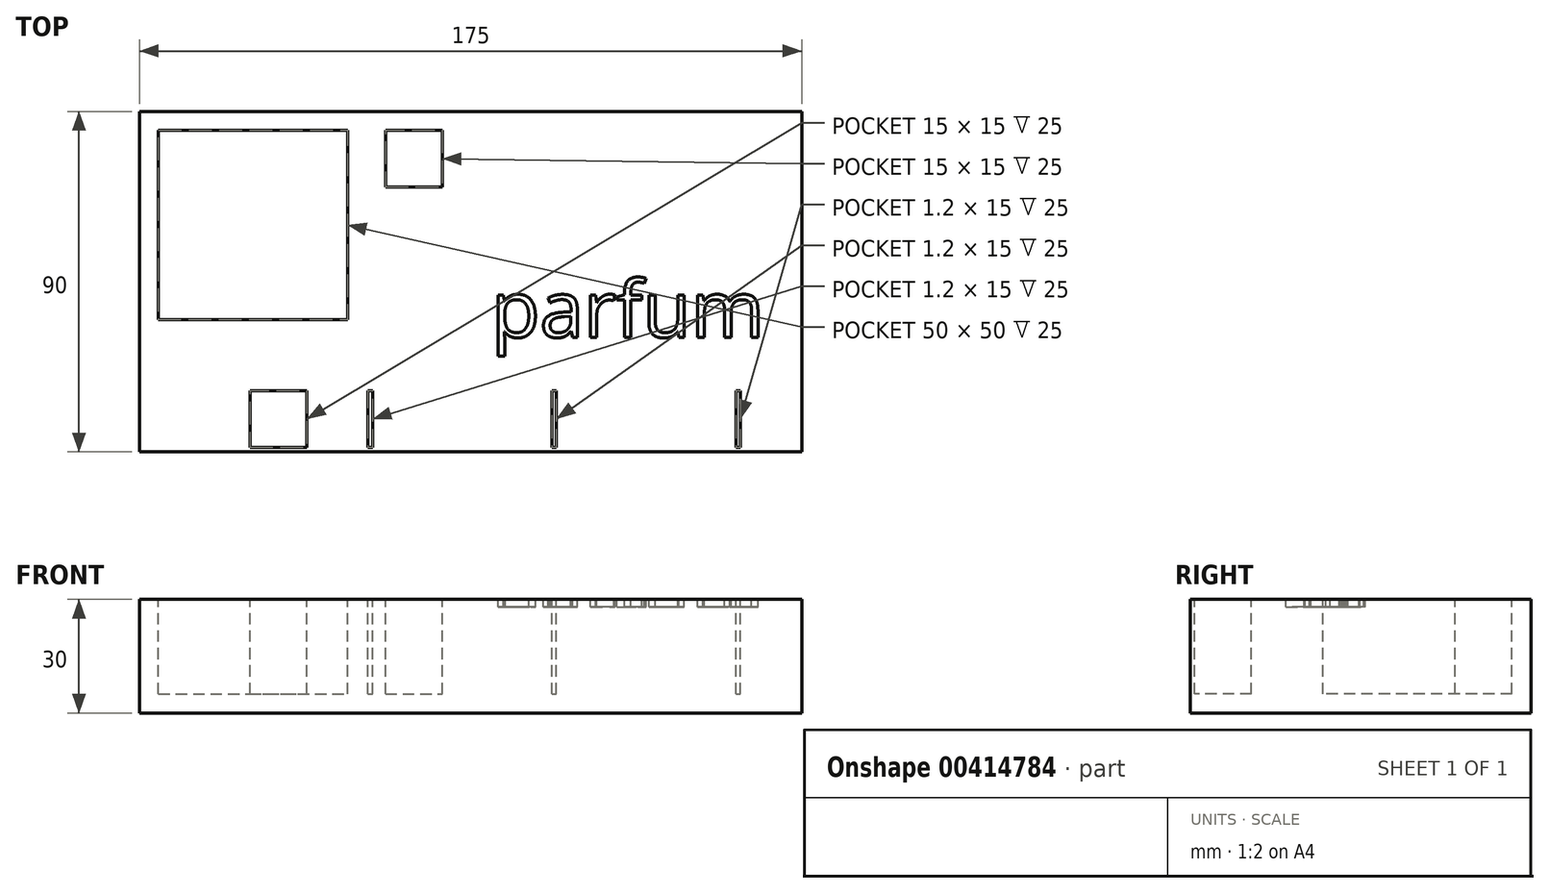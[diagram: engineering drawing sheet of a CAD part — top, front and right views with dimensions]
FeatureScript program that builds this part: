
annotation { "Feature Type Name" : "Feature", "Feature Type Description" : "" }
export const myFeature = defineFeature(function(context is Context, id is Id, definition is map)
    precondition{}
    {
        {
            var Q0;
            Q0=qCreatedBy(makeId("Top.planeOp"),FACE);
            var sketch = newSketch(context, id + "F0", { "sketchPlane" : qUnion([Q0])});
            skLineSegment(sketch, "E0.bottom", {"start": v(0, 0) * mm, "end": v(-175, 0) * mm});
            skLineSegment(sketch, "E0.top", {"start": v(0, -90) * mm, "end": v(-175, -90) * mm});
            skLineSegment(sketch, "E0.left", {"start": v(0, 0) * mm, "end": v(0, -90) * mm});
            skLineSegment(sketch, "E0.right", {"start": v(-175, 0) * mm, "end": v(-175, -90) * mm});
            skSolve(sketch);
        }
        {
            var Q0;
            Q0 = qSketchRegion(id + "F0", true);
            extrude(context, id + "F1", {"entities" : qUnion([Q0]), "depth" : 30 * mm});
        }
        {
            var Q0;
            Q0=makeQuery(id+"F1.opExtrude","CAP_FACE",FACE,{"disambiguationData":[OSD([sQuery(id+"F0.wireOp",EDGE,"E0.bottom"),sQuery(id+"F0.wireOp",EDGE,"E0.top"),sQuery(id+"F0.wireOp",EDGE,"E0.left"),sQuery(id+"F0.wireOp",EDGE,"E0.right")])],"isStart":false});
            var sketch = newSketch(context, id + "F2", { "sketchPlane" : qUnion([Q0])});
            skLineSegment(sketch, "E1.bottom", {"start": v(-175, 0) * mm, "end": v(0, 0) * mm});
            skLineSegment(sketch, "E1.left", {"start": v(-175, 0) * mm, "end": v(-175, -60) * mm});
            skLineSegment(sketch, "E1.right", {"start": v(0, 0) * mm, "end": v(0, -60) * mm});
            skLineSegment(sketch, "E2.bottom", {"start": v(-170, -5) * mm, "end": v(-120, -5) * mm});
            skLineSegment(sketch, "E2.top", {"start": v(-173.8, -88.8) * mm, "end": v(-1.2, -88.8) * mm});
            skLineSegment(sketch, "E2.left", {"start": v(-170, -5) * mm, "end": v(-170, -55) * mm});
            skLineSegment(sketch, "E2.right", {"start": v(-5, -5) * mm, "end": v(-5, -40) * mm});
            skLineSegment(sketch, "E3.top", {"start": v(-163.2, -88.8) * mm, "end": v(-130.8, -88.8) * mm});
            skLineSegment(sketch, "E3.right", {"start": v(-130.8, -73.8) * mm, "end": v(-130.8, -88.8) * mm});
            skLineSegment(sketch, "E4.top", {"start": v(-130.8, -88.8) * mm, "end": v(-114.6, -88.8) * mm});
            skLineSegment(sketch, "E4.right", {"start": v(-114.6, -73.8) * mm, "end": v(-114.6, -88.8) * mm});
            skLineSegment(sketch, "E5.top", {"start": v(-140, -88.8) * mm, "end": v(-125, -88.8) * mm});
            skLineSegment(sketch, "E6.top", {"start": v(-125, -88.8) * mm, "end": v(-110, -88.8) * mm});
            skLineSegment(sketch, "E7.top", {"start": v(-110, -88.8) * mm, "end": v(-81, -88.8) * mm});
            skLineSegment(sketch, "E7.right", {"start": v(-81, -73.8) * mm, "end": v(-81, -88.8) * mm});
            skLineSegment(sketch, "E8.top", {"start": v(-81, -88.8) * mm, "end": v(-66, -88.8) * mm});
            skLineSegment(sketch, "E8.right", {"start": v(-66, -73.8) * mm, "end": v(-66, -88.8) * mm});
            skLineSegment(sketch, "E9.top", {"start": v(-95, -88.8) * mm, "end": v(-66, -88.8) * mm});
            skLineSegment(sketch, "E10.top", {"start": v(-81, -88.8) * mm, "end": v(-64.8, -88.8) * mm});
            skLineSegment(sketch, "E10.right", {"start": v(-64.8, -73.8) * mm, "end": v(-64.8, -88.8) * mm});
            skLineSegment(sketch, "E11.top", {"start": v(-64.8, -88.8) * mm, "end": v(-50, -88.8) * mm});
            skLineSegment(sketch, "E12.top", {"start": v(-50, -88.8) * mm, "end": v(-32.4, -88.8) * mm});
            skLineSegment(sketch, "E12.right", {"start": v(-32.4, -73.8) * mm, "end": v(-32.4, -88.8) * mm});
            skLineSegment(sketch, "E13.top", {"start": v(-32.4, -88.8) * mm, "end": v(-17.4, -88.8) * mm});
            skLineSegment(sketch, "E13.right", {"start": v(-17.4, -73.8) * mm, "end": v(-17.4, -88.8) * mm});
            skLineSegment(sketch, "E14.bottom", {"start": v(-173.8, -88.8) * mm, "end": v(-5, -88.8) * mm});
            skLineSegment(sketch, "E14.top", {"start": v(-173.8, -73.8) * mm, "end": v(-1.2, -73.8) * mm});
            skLineSegment(sketch, "E15.right", {"start": v(-120, -5) * mm, "end": v(-120, -55) * mm});
            skLineSegment(sketch, "E16.right", {"start": v(-110, -5) * mm, "end": v(-110, -20) * mm});
            skLineSegment(sketch, "E17.top", {"start": v(-110, -5) * mm, "end": v(-95, -5) * mm});
            skLineSegment(sketch, "E17.left", {"start": v(-110, -20) * mm, "end": v(-110, -5) * mm});
            skLineSegment(sketch, "E17.right", {"start": v(-95, -20) * mm, "end": v(-95, -5) * mm});
            skLineSegment(sketch, "E18.top", {"start": v(-5, -5) * mm, "end": v(-40, -5) * mm});
            skLineSegment(sketch, "E18.left", {"start": v(-5, -40) * mm, "end": v(-5, -5) * mm});
            skLineSegment(sketch, "E18.right", {"start": v(-40, -40) * mm, "end": v(-40, -5) * mm});
            skLineSegment(sketch, "E19.right", {"start": v(-50, -40) * mm, "end": v(-50, -5) * mm});
            skLineSegment(sketch, "E20.top", {"start": v(-50, -5) * mm, "end": v(-85, -5) * mm});
            skLineSegment(sketch, "E20.right", {"start": v(-85, -40) * mm, "end": v(-85, -5) * mm});
            skLineSegment(sketch, "E21.top", {"start": v(-170, -55) * mm, "end": v(-120, -55) * mm});
            skLineSegment(sketch, "E22.top", {"start": v(-110, -20) * mm, "end": v(-95, -20) * mm});
            skLineSegment(sketch, "E22.right", {"start": v(-95, -5) * mm, "end": v(-95, -20) * mm});
            skLineSegment(sketch, "E23.trimOffspring", {"start": v(-85, -5) * mm, "end": v(-50, -5) * mm});
            skLineSegment(sketch, "E24.trimOffspring", {"start": v(-40, -5) * mm, "end": v(-5, -5) * mm});
            skLineSegment(sketch, "E25.top", {"start": v(-85, -40) * mm, "end": v(-50, -40) * mm});
            skLineSegment(sketch, "E25.left", {"start": v(-85, -5) * mm, "end": v(-85, -40) * mm});
            skLineSegment(sketch, "E25.right", {"start": v(-50, -5) * mm, "end": v(-50, -40) * mm});
            skPoint(sketch, "E26.orphan", {"position": v(-50, -60) * mm});
            skLineSegment(sketch, "E27.top", {"start": v(-40, -40) * mm, "end": v(-5, -40) * mm});
            skLineSegment(sketch, "E27.left", {"start": v(-40, -5) * mm, "end": v(-40, -40) * mm});
            skLineSegment(sketch, "E28", {"start": v(-1.2, -73.8) * mm, "end": v(-1.2, -88.8) * mm});
            skLineSegment(sketch, "E29", {"start": v(-173.8, -73.8) * mm, "end": v(-173.8, -88.8) * mm});
            skPoint(sketch, "E30.orphan", {"position": v(-5, -73.8) * mm});
            skLineSegment(sketch, "E31", {"start": v(-16.2, -73.8) * mm, "end": v(-16.2, -88.8) * mm});
            skLineSegment(sketch, "E32", {"start": v(-33.6, -73.8) * mm, "end": v(-33.6, -88.8) * mm});
            skLineSegment(sketch, "E33", {"start": v(-48.6, -73.8) * mm, "end": v(-48.6, -88.8) * mm});
            skLineSegment(sketch, "E34", {"start": v(-49.8, -73.8) * mm, "end": v(-49.8, -88.8) * mm});
            skLineSegment(sketch, "E35", {"start": v(-82.2, -73.8) * mm, "end": v(-82.2, -88.8) * mm});
            skLineSegment(sketch, "E36", {"start": v(-97.2, -73.8) * mm, "end": v(-97.2, -88.8) * mm});
            skLineSegment(sketch, "E37", {"start": v(-98.4, -73.8) * mm, "end": v(-98.4, -88.8) * mm});
            skLineSegment(sketch, "E38", {"start": v(-113.4, -73.8) * mm, "end": v(-113.4, -88.8) * mm});
            skLineSegment(sketch, "E39", {"start": v(-145.8, -73.8) * mm, "end": v(-145.8, -88.8) * mm});
            skLineSegment(sketch, "E40", {"start": v(-129.6, -73.8) * mm, "end": v(-129.6, -88.8) * mm});
            skLineSegment(sketch, "E41", {"start": v(-147, -88.8) * mm, "end": v(-147, -73.8) * mm});
            skLineSegment(sketch, "E42", {"start": v(-162, -88.8) * mm, "end": v(-162, -73.8) * mm});
            skLineSegment(sketch, "E43", {"start": v(-163.2, 0) * mm, "end": v(-163.2, -90.3) * mm});
            skSolve(sketch);
        }
        {
            var Q0;
            {var subQ0=sQuery(id+"F2.wireOp",EDGE,"E3.right");Q0=makeQuery(id+"F2.imprint","IMPRINT",FACE,{"disambiguationData":[TD([[makeQuery(id+"F2.imprint","IMPRINT",EDGE,{"derivedFrom":subQ0}),-1.0]])]});}
            var Q1;
            {var subQ0=sQuery(id+"F2.wireOp",EDGE,"E4.right");Q1=makeQuery(id+"F2.imprint","IMPRINT",FACE,{"disambiguationData":[TD([[makeQuery(id+"F2.imprint","IMPRINT",EDGE,{"derivedFrom":subQ0}),1.0]])]});}
            var Q2;
            {var subQ0=sQuery(id+"F2.wireOp",EDGE,"E7.left");Q2=makeQuery(id+"F2.imprint","IMPRINT",FACE,{"disambiguationData":[TD([[makeQuery(id+"F2.imprint","IMPRINT",EDGE,{"derivedFrom":subQ0}),1.0]])]});}
            var Q3;
            {var subQ0=sQuery(id+"F2.wireOp",EDGE,"E8.right");Q3=makeQuery(id+"F2.imprint","IMPRINT",FACE,{"disambiguationData":[TD([[makeQuery(id+"F2.imprint","IMPRINT",EDGE,{"derivedFrom":subQ0}),1.0]])]});}
            var Q4;
            {var subQ0=sQuery(id+"F2.wireOp",EDGE,"E12.left");Q4=makeQuery(id+"F2.imprint","IMPRINT",FACE,{"disambiguationData":[TD([[makeQuery(id+"F2.imprint","IMPRINT",EDGE,{"derivedFrom":subQ0}),1.0]])]});}
            var Q5;
            {var subQ0=sQuery(id+"F2.wireOp",EDGE,"E13.right");Q5=makeQuery(id+"F2.imprint","IMPRINT",FACE,{"disambiguationData":[TD([[makeQuery(id+"F2.imprint","IMPRINT",EDGE,{"derivedFrom":subQ0}),1.0]])]});}
            var Q6;
            Q6=makeQuery(id+"F2.imprint","IMPRINT",FACE,{"disambiguationData":[TD([[makeQuery(id+"F2.imprint","IMPRINT",EDGE,{"derivedFrom":sQuery(id+"F2.wireOp",EDGE,"E24.trimOffspring")}),-1.0]])]});
            var Q7;
            Q7=makeQuery(id+"F2.imprint","IMPRINT",FACE,{"disambiguationData":[TD([[makeQuery(id+"F2.imprint","IMPRINT",EDGE,{"derivedFrom":sQuery(id+"F2.wireOp",EDGE,"E23.trimOffspring")}),-1.0]])]});
            var Q8;
            Q8=makeQuery(id+"F2.imprint","IMPRINT",FACE,{"disambiguationData":[TD([[makeQuery(id+"F2.imprint","IMPRINT",EDGE,{"derivedFrom":sQuery(id+"F2.wireOp",EDGE,"E22.top")}),1.0]])]});
            var Q9;
            Q9=makeQuery(id+"F2.imprint","IMPRINT",FACE,{"disambiguationData":[TD([[makeQuery(id+"F2.imprint","IMPRINT",EDGE,{"derivedFrom":sQuery(id+"F2.wireOp",EDGE,"E2.bottom")}),-1.0]])]});
            extrude(context, id + "F3", {"entities" : qUnion([Q0, Q1, Q2, Q3, Q4, Q5, Q6, Q7, Q8, Q9]), "operationType" : NewBodyOperationType.REMOVE, "oppositeDirection" : true, "depth" : 25 * mm});
        }
        {
            var Q0;
            Q0=makeQuery(id+"F1.opExtrude","CAP_FACE",FACE,{"disambiguationData":[OSD([sQuery(id+"F0.wireOp",EDGE,"E0.bottom"),sQuery(id+"F0.wireOp",EDGE,"E0.top"),sQuery(id+"F0.wireOp",EDGE,"E0.left"),sQuery(id+"F0.wireOp",EDGE,"E0.right")])],"isStart":false});
            var sketch = newSketch(context, id + "F4", { "sketchPlane" : qUnion([Q0])});
            skSolve(sketch);
        }
        {
            var Q0;
            {var subQ3=sQuery(id+"F0.wireOp",EDGE,"E0.bottom");Q0=makeQuery(id+"F4.imprint","IMPRINT",FACE,{"disambiguationData":[TD([[makeQuery(id+"F4.imprint","IMPRINT",EDGE,{"derivedFrom":makeQuery(id+"F1.opExtrude","CAP_EDGE",EDGE,{"disambiguationData":[OSD([subQ3])],"isStart":false})}),1.0]])]});}
            var sketch = newSketch(context, id + "F5", { "sketchPlane" : qUnion([Q0])});
            skText(sketch, "E44", { "text": "parfum\n", "fontName": "OpenSans-Regular.ttf"});
            const initialGuessF5  = {"E44": [-0.08198, -0.0597, 1, 0, 0.015]};
            skSetInitialGuess(sketch, initialGuessF5);
            skSolve(sketch);
        }
        {
            var Q0;
            Q0 = qSketchRegion(id + "F5", true);
            extrude(context, id + "F6", {"entities" : qUnion([Q0]), "operationType" : NewBodyOperationType.REMOVE, "oppositeDirection" : true, "depth" : 2 * mm});
        }
    });
